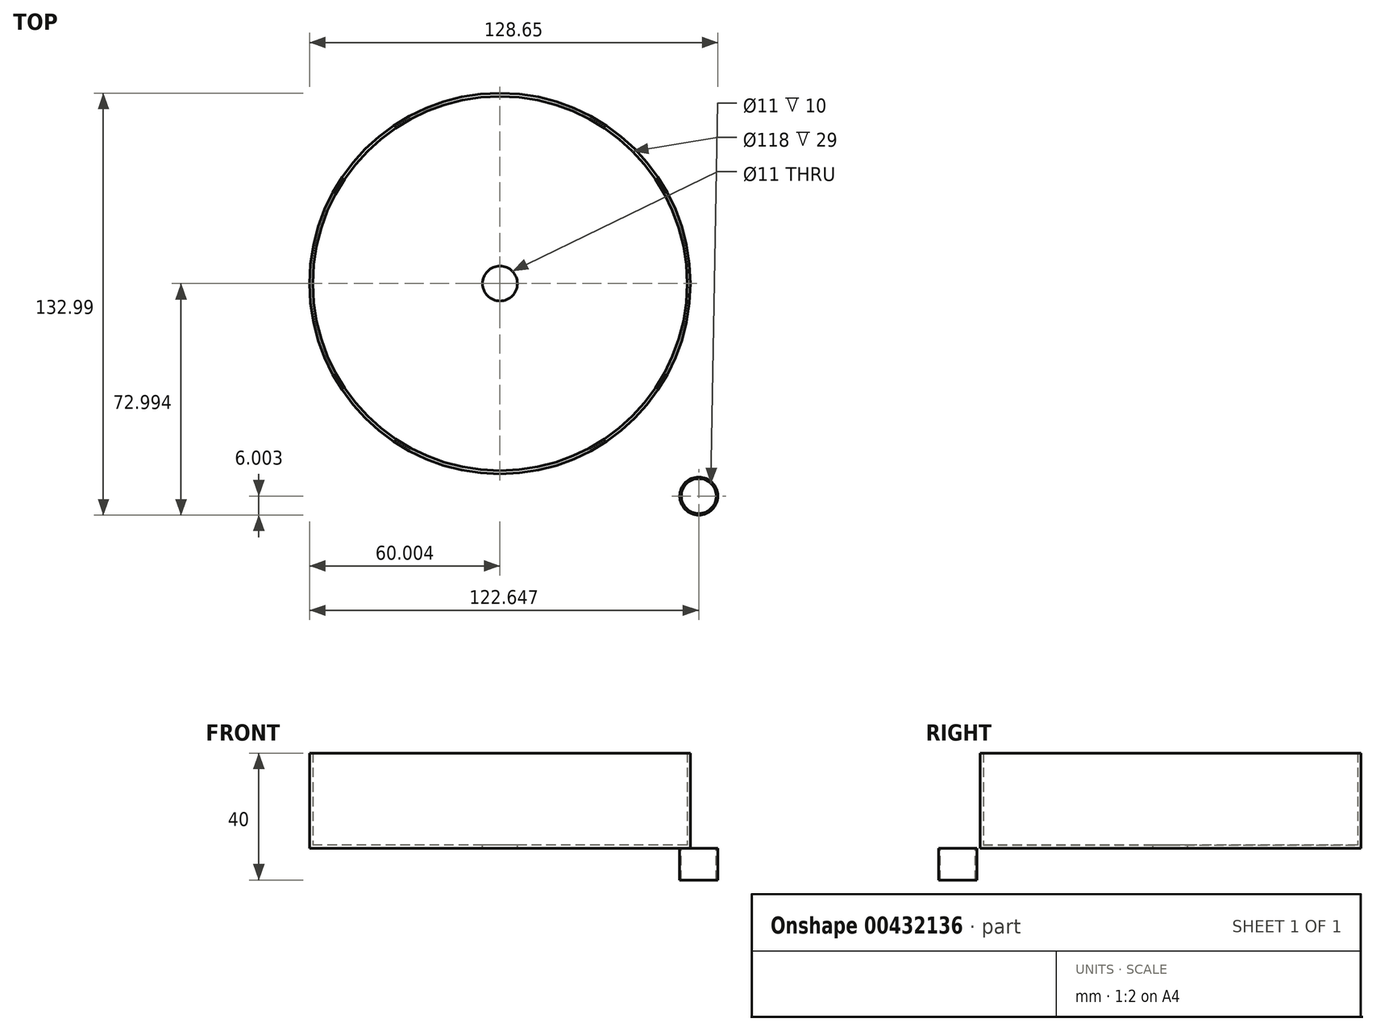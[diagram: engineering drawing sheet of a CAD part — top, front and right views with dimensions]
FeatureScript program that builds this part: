
annotation { "Feature Type Name" : "Feature", "Feature Type Description" : "" }
export const myFeature = defineFeature(function(context is Context, id is Id, definition is map)
    precondition{}
    {
        {
            var Q0;
            Q0=qCreatedBy(makeId("Top.planeOp"),FACE);
            var sketch = newSketch(context, id + "F0", { "sketchPlane" : qUnion([Q0])});
            skCircle(sketch, "E0", {"center": v(-24.19, 25.2) * mm, "radius": 60 * mm});
            skSolve(sketch);
        }
        {
            var Q0;
            Q0=makeQuery(id+"F0.imprint","IMPRINT",FACE,{"disambiguationData":[TD([[makeQuery(id+"F0.imprint","IMPRINT",EDGE,{"derivedFrom":sQuery(id+"F0.wireOp",EDGE,"E0")}),1.0]])]});
            extrude(context, id + "F1", {"entities" : qUnion([Q0]), "depth" : 30 * mm});
        }
        {
            var Q0;
            Q0=makeQuery(id+"F1.opExtrude","CAP_FACE",FACE,{"disambiguationData":[OSD([sQuery(id+"F0.wireOp",EDGE,"E0")])],"isStart":false});
            shell(context, id + "F2", {"entities" : qUnion([Q0]), "thickness" : 1 * mm});
        }
        {
            var Q0;
            {var subQ0=sQuery(id+"F0.wireOp",EDGE,"E0");Q0=makeQuery(id+"F2.opShell","OFFSET_FACE",FACE,{"disambiguationData":[OSD([subQ0]),TDD([makeQuery(id+"F1.opExtrude","CAP_FACE",FACE,{"disambiguationData":[OSD([subQ0])],"isStart":true})])]});}
            var sketch = newSketch(context, id + "F3", { "sketchPlane" : qUnion([Q0])});
            skCircle(sketch, "E1", {"center": v(-24.19, 25.2) * mm, "radius": 6 * mm});
            skSolve(sketch);
        }
        {
            var Q0;
            Q0=sQuery(id+"F3.wireOp",VERTEX,"E1.center");
            var Q1;
            Q1=makeQuery(id+"F1.opExtrude","SWEPT_BODY",BODY,{"disambiguationData":[OSD([sQuery(id+"F0.wireOp",EDGE,"E0")])]});
            hole(context, id + "F4", {"style" : HoleStyle.SIMPLE, "endStyle" : HoleEndStyle.THROUGH, "holeDiameter" : 11 * mm, "isTappedThrough" : true, "tappedDepth" : 12 * mm, "tapClearance" : 3, "locations" : qUnion([Q0]), "scope" : qUnion([Q1])});
        }
        {
            var Q0;
            Q0=qCreatedBy(makeId("Top.planeOp"),FACE);
            var sketch = newSketch(context, id + "F5", { "sketchPlane" : qUnion([Q0])});
            skCircle(sketch, "E2", {"center": v(38.46, -41.8) * mm, "radius": 6 * mm});
            skSolve(sketch);
        }
        {
            var Q0;
            Q0 = qSketchRegion(id + "F5", true);
            extrude(context, id + "F6", {"entities" : qUnion([Q0]), "oppositeDirection" : true, "depth" : 10 * mm});
        }
        {
            var Q0;
            Q0=sQuery(id+"F5.wireOp",VERTEX,"E2.center");
            var Q1;
            Q1=makeQuery(id+"F6.opExtrude","SWEPT_BODY",BODY,{"disambiguationData":[OSD([sQuery(id+"F5.wireOp",EDGE,"E2")])]});
            hole(context, id + "F7", {"style" : HoleStyle.SIMPLE, "endStyle" : HoleEndStyle.THROUGH, "holeDiameter" : 11 * mm, "isTappedThrough" : true, "tappedDepth" : 12 * mm, "tapClearance" : 3, "locations" : qUnion([Q0]), "scope" : qUnion([Q1]), "majorDiameter" : 5 * mm});
        }
    });
